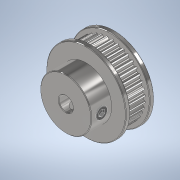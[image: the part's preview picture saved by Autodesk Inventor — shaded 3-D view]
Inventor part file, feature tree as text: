
AUTODESK INVENTOR PART (.ipt)
format: ipt  version: 2022 (Build 260153000, 153)  size: 633,344 bytes
history: native  units: in
note: dims shown in document units (in); Inventor stores cm internally (conversion verified against a paired STEP export)
features: sketch x5, other x3, extrude x2, plane x2, hole x2, chamfer x1, pattern_circular x1, projected_geometry x1
ambient origin geometry x8: Origin, YZ Plane, XZ Plane, XY Plane, X Axis, Y Axis, Z Axis, Center Point
bodies: Solid1 (feature_tree), Solid2 (feature_tree), Solid3 (feature_tree)
feature tree (17):
  other  "Pulley_1:1"
  extrude  "Extrusion1"  Depth=0.0079in TaperAngle=45.0deg
  plane  "Work Plane1"
  hole  "Hole2"  [1 undecoded]
  plane  "Work Plane2"
  hole  "Hole1"  [1 undecoded]
  chamfer  "Chamfer1"  [1 undecoded]
  extrude  "Extrusion2"  [1 undecoded]
  pattern_circular  "Circular Pattern1"  [2 undecoded]
  sketch  "Sketch1"  dims[d0=0.2815in d1=0.0in]
  sketch  "Sketch2"  dims[d2=0.1969in d3=0.75in d4=0.375in d5=0.25in d6=0.5635in d7=1.0in d8=0.8108in]
  sketch  "Sketch3"  dims[d9=0.1312in d10=0.75in d11=0.375in d12=0.25in d13=0.5635in d14=1.0in d15=0.8108in]
  sketch  "Sketch4"  dims[d16=0.1312in d17=0.75in d18=0.375in d19=0.25in d20=0.5635in d21=1.0in d22=0.8108in d23=0.0079in d24=0.0079in d25=45.0deg]
  sketch  "Sketch5"  dims[d26=1.0in d27=0.0in d28=15.748in d29=360.0deg]
  projected_geometry  "Projected Loop1"
  other  "Screw v1_1:1"
  other  "Screw v1 (1)_1:1"
note: 6 required parameter values undecoded (feature->parameter linkage not recoverable at this tier; creation-order binding heuristic only, values carry confidence <= 0.55)
